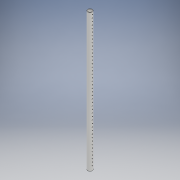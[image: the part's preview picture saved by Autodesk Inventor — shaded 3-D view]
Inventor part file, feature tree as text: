
AUTODESK INVENTOR PART (.ipt)
format: ipt  version: 2018 (Build 220112000, 112)  size: 312,832 bytes
history: native  units: mm
features: sketch x2, extrude x1, hole x1, projected_geometry x1
ambient origin geometry x8: Origin, YZ Plane, XZ Plane, XY Plane, X Axis, Y Axis, Z Axis, Center Point
bodies: Solid1 (feature_tree)
feature tree (5):
  extrude  "Extrusion1"  Depth=35.052mm
  hole  "Hole1"  [1 undecoded]
  sketch  "Sketch1"  dims[d0=42.164mm d1=35.052mm]
  sketch  "Sketch2"  dims[d2=1225.0mm d3=0.0mm d4=38.52075mm d5=440.0mm d7=27.15mm d8=10.0mm d10=10.0mm d12=6.35mm d13=6.0mm d14=4.0mm d15=2.0mm d16=90.0deg d17=8.0mm d18=20.594885mm]
  projected_geometry  "Projected Loop1"
note: 1 required parameter value undecoded (feature->parameter linkage not recoverable at this tier; creation-order binding heuristic only, values carry confidence <= 0.55)
